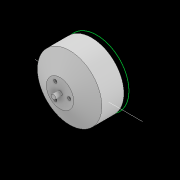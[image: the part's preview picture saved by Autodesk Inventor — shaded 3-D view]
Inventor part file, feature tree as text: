
AUTODESK INVENTOR PART (.ipt)
format: ipt  version: 2022.2 (Build 262287010, 287A)  size: 178,688 bytes
history: native  units: mm
features: sketch x9, extrude x5, hole x3, chamfer x2
ambient origin geometry x8: Origin, YZ Plane, XZ Plane, XY Plane, X Axis, Y Axis, Z Axis, Center Point
bodies: Solid1 (feature_tree)
feature tree (19):
  sketch  "Sketch1"  dims[d0=59.0mm d1=32.0mm]
  extrude  "Extrusion1"  Depth=32.0mm
  extrude  "Extrusion2"  Depth=17.0mm
  extrude  "Extrusion3"  Depth=40.0mm TaperAngle=360.0deg
  hole  "Hole1"  [1 undecoded]
  chamfer  "Chamfer1"  Distance=42.5mm
  extrude  "Magnet"  Depth=3.0mm TaperAngle=0.0deg
  chamfer  "Chamfer2"  Distance=25.0mm
  sketch  "Sketch7"  dims[d22=3.0mm]
  hole  "Hole2"  [1 undecoded]
  hole  "Hole3"  [1 undecoded]
  extrude  "Extrusion5"  Depth=4.5mm TaperAngle=45.0deg
  sketch  "Sketch9"  dims[d28=20.594885mm d29=25.0mm d30=8.8mm d31=17.0mm d32=45.0deg d33=2.0mm d34=0.0mm d35=4.5mm d36=7.5mm d37=45.0deg d38=3.0mm d39=6.0mm d40=4.0mm d41=2.0mm d42=90.0deg d43=4.0mm d44=20.594885mm d45=2.5mm d46=6.0mm d47=4.0mm d48=2.0mm d49=90.0deg d50=3.0mm d51=20.594885mm d52=0.5mm d53=0.0mm]
  sketch  "Sketch2"  dims[d2=25.0mm d3=17.0mm]
  sketch  "Sketch3"  dims[d4=45.0deg d6=40.0mm d8=360.0deg]
  sketch  "Sketch4"  dims[d10=30.0mm d12=360.0deg d14=6.0mm]
  sketch  "Sketch5"  dims[d15=4.0mm d16=42.5mm d17=0.0mm]
  sketch  "Sketch6"  dims[d18=6.0mm d19=0.0mm d20=3.0mm d21=0.0mm]
  sketch  "Sketch8"  dims[d23=6.0mm d24=4.0mm d25=2.0mm d26=90.0deg d27=5.0mm]
note: 3 required parameter values undecoded (feature->parameter linkage not recoverable at this tier; creation-order binding heuristic only, values carry confidence <= 0.55)
